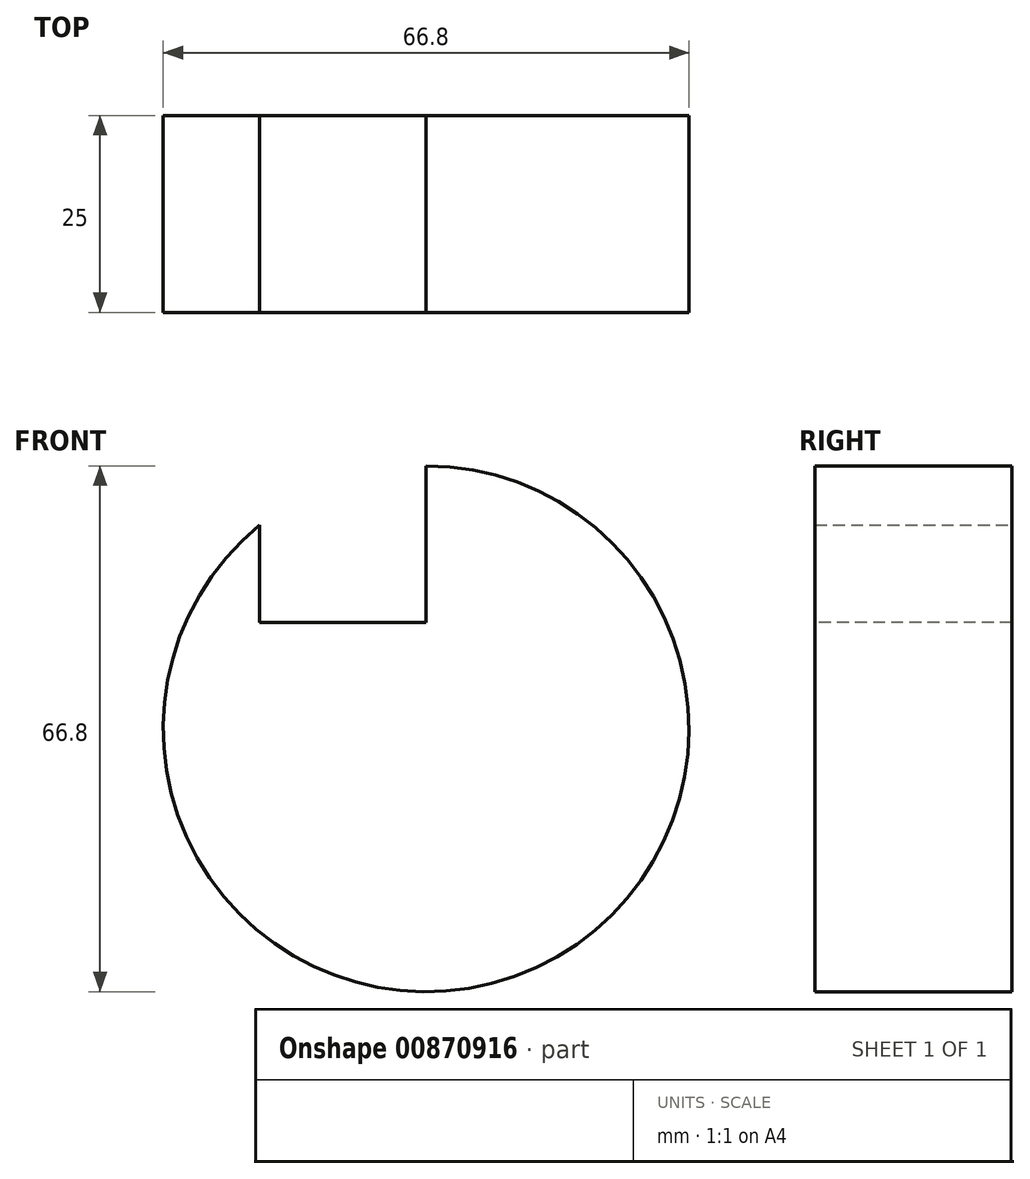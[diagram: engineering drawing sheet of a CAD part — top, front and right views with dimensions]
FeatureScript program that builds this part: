
annotation { "Feature Type Name" : "Feature", "Feature Type Description" : "" }
export const myFeature = defineFeature(function(context is Context, id is Id, definition is map)
    precondition{}
    {
        {
            var Q0;
            Q0=qCreatedBy(makeId("Front.planeOp"),FACE);
            var sketch = newSketch(context, id + "F0", { "sketchPlane" : qUnion([Q0])});
            skCircle(sketch, "E0", {"center": v(0, 0) * mm, "radius": 33.4 * mm});
            skSolve(sketch);
        }
        {
            var Q0;
            Q0=makeQuery(id+"F0.imprint","IMPRINT",FACE,{"disambiguationData":[TD([[makeQuery(id+"F0.imprint","IMPRINT",EDGE,{"derivedFrom":sQuery(id+"F0.wireOp",EDGE,"E0")}),1.0]])]});
            var Q1;
            Q1 = qSketchRegion(id + "F0", true);
            extrude(context, id + "F1", {"entities" : qUnion([Q0, Q1]), "depth" : 25 * mm, "offsetDistance" : 25 * mm});
        }
        {
            var Q0;
            Q0=makeQuery(id+"F1.opExtrude","CAP_FACE",FACE,{"disambiguationData":[OSD([sQuery(id+"F0.wireOp",EDGE,"E0")])],"isStart":false});
            var sketch = newSketch(context, id + "F2", { "sketchPlane" : qUnion([Q0])});
            skLineSegment(sketch, "E1.bottom", {"start": v(0, 33.4) * mm, "end": v(-42.27, 33.4) * mm});
            skLineSegment(sketch, "E1.top", {"start": v(0, 50.7) * mm, "end": v(-42.27, 50.7) * mm});
            skLineSegment(sketch, "E1.left", {"start": v(0, 33.4) * mm, "end": v(0, 50.7) * mm});
            skLineSegment(sketch, "E1.right", {"start": v(-42.27, 33.4) * mm, "end": v(-42.27, 50.7) * mm});
            skLineSegment(sketch, "E2.bottom", {"start": v(0, 13.49) * mm, "end": v(0, 13.49) * mm});
            skLineSegment(sketch, "E2.top", {"start": v(0, 0) * mm, "end": v(0, 0) * mm});
            skLineSegment(sketch, "E2.left", {"start": v(0, 13.49) * mm, "end": v(0, 0) * mm});
            skLineSegment(sketch, "E2.right", {"start": v(0, 13.49) * mm, "end": v(0, 0) * mm});
            skLineSegment(sketch, "E3.bottom", {"start": v(-8.67, 50.7) * mm, "end": v(-21.13, 50.7) * mm});
            skLineSegment(sketch, "E3.top", {"start": v(-8.67, 50.7) * mm, "end": v(-21.13, 50.7) * mm});
            skLineSegment(sketch, "E3.left", {"start": v(-8.67, 50.7) * mm, "end": v(-8.67, 50.7) * mm});
            skLineSegment(sketch, "E3.right", {"start": v(-21.13, 50.7) * mm, "end": v(-21.13, 50.7) * mm});
            skPoint(sketch, "E4.oppositeSnap0", {"position": v(-21.13, 33.4) * mm});
            skLineSegment(sketch, "E4.bottom", {"start": v(-21.13, 33.4) * mm, "end": v(-21.13, 33.4) * mm});
            skLineSegment(sketch, "E4.top", {"start": v(-21.13, 72.38) * mm, "end": v(-21.13, 72.38) * mm});
            skLineSegment(sketch, "E4.left", {"start": v(-21.13, 33.4) * mm, "end": v(-21.13, 72.38) * mm});
            skLineSegment(sketch, "E4.right", {"start": v(-21.13, 33.4) * mm, "end": v(-21.13, 72.38) * mm});
            skLineSegment(sketch, "E5.bottom", {"start": v(-21.13, 33.4) * mm, "end": v(0, 33.4) * mm});
            skLineSegment(sketch, "E5.top", {"start": v(-21.13, 13.49) * mm, "end": v(0, 13.49) * mm});
            skLineSegment(sketch, "E5.left", {"start": v(-21.13, 33.4) * mm, "end": v(-21.13, 13.49) * mm});
            skLineSegment(sketch, "E5.right", {"start": v(0, 33.4) * mm, "end": v(0, 13.49) * mm});
            skSolve(sketch);
        }
        {
            var Q0;
            Q0 = qSketchRegion(id + "F2", true);
            extrude(context, id + "F3", {"entities" : qUnion([Q0]), "operationType" : NewBodyOperationType.REMOVE, "oppositeDirection" : true, "depth" : 25 * mm, "offsetDistance" : 25 * mm});
        }
    });
